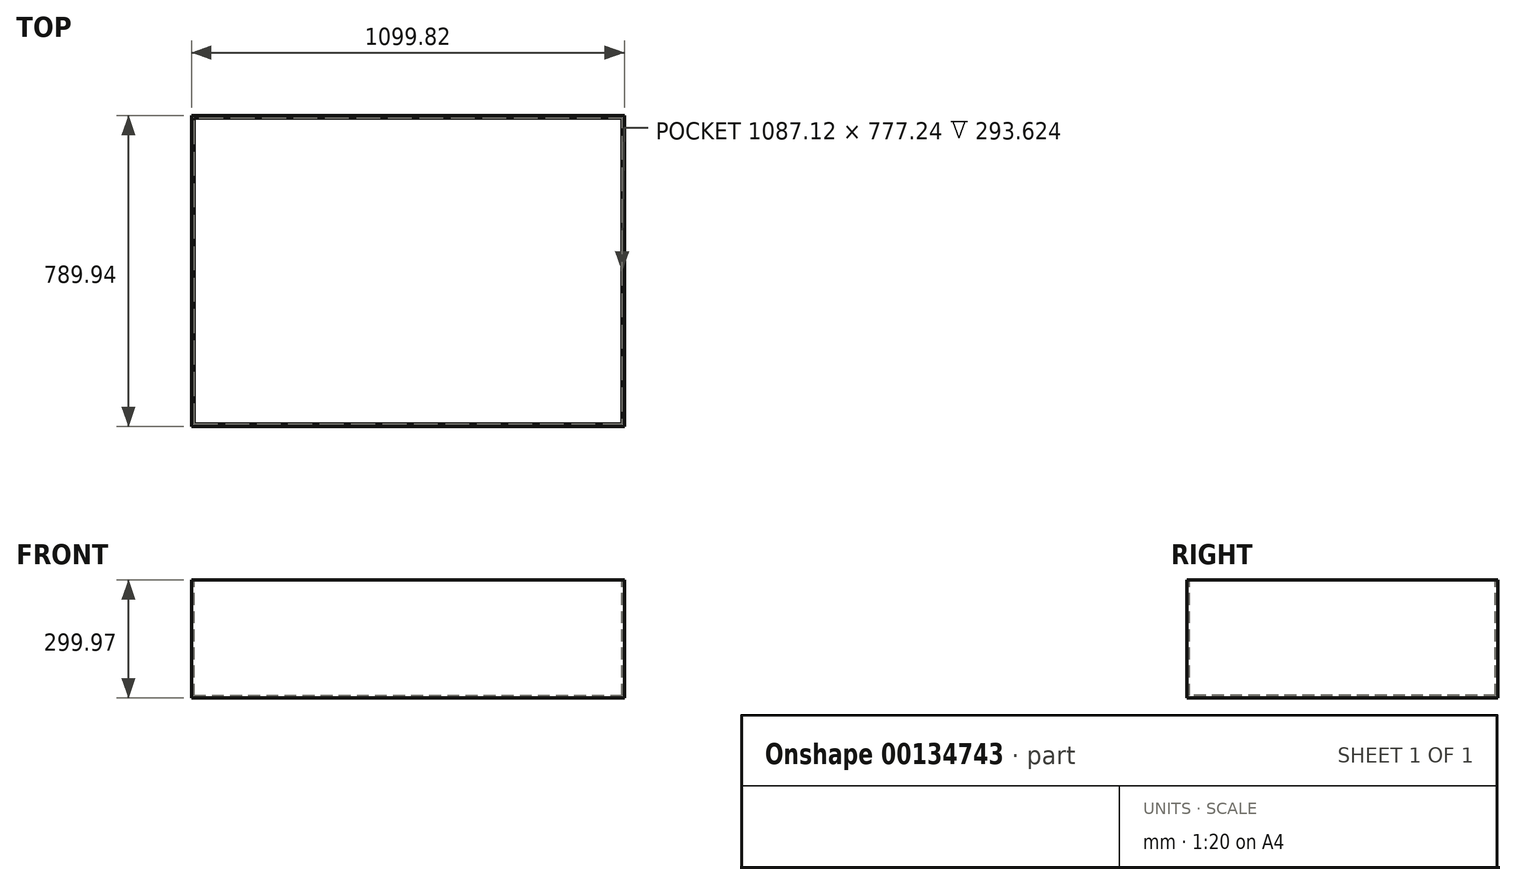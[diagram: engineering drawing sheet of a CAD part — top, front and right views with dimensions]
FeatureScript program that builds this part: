
annotation { "Feature Type Name" : "Feature", "Feature Type Description" : "" }
export const myFeature = defineFeature(function(context is Context, id is Id, definition is map)
    precondition{}
    {
        {
            var Q0;
            Q0=qCreatedBy(makeId("Top.planeOp"),FACE);
            var sketch = newSketch(context, id + "F0", { "sketchPlane" : qUnion([Q0])});
            skLineSegment(sketch, "E0.bottom", {"start": v(0, 789.94) * mm, "end": v(1099.82, 789.94) * mm});
            skLineSegment(sketch, "E0.top", {"start": v(0, 0) * mm, "end": v(1099.82, 0) * mm});
            skLineSegment(sketch, "E0.left", {"start": v(0, 789.94) * mm, "end": v(0, 0) * mm});
            skLineSegment(sketch, "E0.right", {"start": v(1099.82, 789.94) * mm, "end": v(1099.82, 0) * mm});
            skSolve(sketch);
        }
        {
            var Q0;
            Q0 = qSketchRegion(id + "F0", true);
            extrude(context, id + "F1", {"entities" : qUnion([Q0]), "oppositeDirection" : true, "depth" : 299.97 * mm});
        }
        {
            var Q0;
            Q0=makeQuery(id+"F1.opExtrude","CAP_FACE",FACE,{"disambiguationData":[OSD([sQuery(id+"F0.wireOp",EDGE,"E0.bottom"),sQuery(id+"F0.wireOp",EDGE,"E0.top"),sQuery(id+"F0.wireOp",EDGE,"E0.left"),sQuery(id+"F0.wireOp",EDGE,"E0.right")])],"isStart":true});
            shell(context, id + "F2", {"entities" : qUnion([Q0]), "thickness" : 6.35 * mm});
        }
    });
